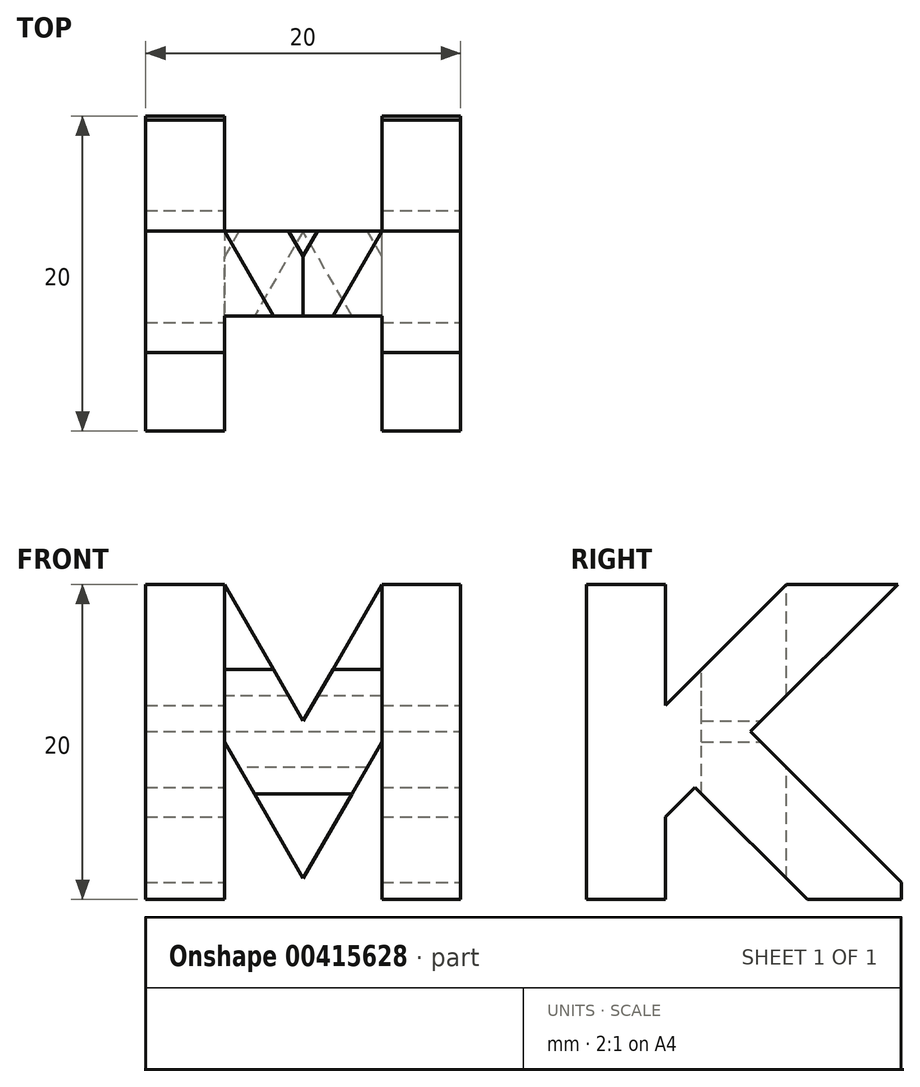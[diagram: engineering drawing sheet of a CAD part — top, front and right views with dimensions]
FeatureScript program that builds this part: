
annotation { "Feature Type Name" : "Feature", "Feature Type Description" : "" }
export const myFeature = defineFeature(function(context is Context, id is Id, definition is map)
    precondition{}
    {
        {
            var Q0;
            Q0=qCreatedBy(makeId("Front.planeOp"),FACE);
            var sketch = newSketch(context, id + "F0", { "sketchPlane" : qUnion([Q0])});
            skPoint(sketch, "E0.middle", {"position": v(0, 0) * mm});
            skLineSegment(sketch, "E1.bottom", {"start": v(-10, -10) * mm, "end": v(-5, -10) * mm});
            skLineSegment(sketch, "E1.top", {"start": v(-10, 10) * mm, "end": v(-5, 10) * mm});
            skLineSegment(sketch, "E1.left", {"start": v(-10, -10) * mm, "end": v(-10, 10) * mm});
            skLineSegment(sketch, "E1.right", {"start": v(-5, -10) * mm, "end": v(-5, 10) * mm});
            skLineSegment(sketch, "E2.bottom", {"start": v(10, 10) * mm, "end": v(5, 10) * mm});
            skLineSegment(sketch, "E2.top", {"start": v(10, -10) * mm, "end": v(5, -10) * mm});
            skLineSegment(sketch, "E2.left", {"start": v(10, 10) * mm, "end": v(10, -10) * mm});
            skLineSegment(sketch, "E2.right", {"start": v(5, 10) * mm, "end": v(5, -10) * mm});
            skLineSegment(sketch, "E3", {"start": v(5, 10) * mm, "end": v(0, 1.34) * mm});
            skLineSegment(sketch, "E4", {"start": v(0, 1.34) * mm, "end": v(-5, 10) * mm});
            skLineSegment(sketch, "E5", {"start": v(5, 0) * mm, "end": v(0, -8.66) * mm});
            skLineSegment(sketch, "E6", {"start": v(0, -8.66) * mm, "end": v(-5, 0) * mm});
            skSolve(sketch);
        }
        {
            var Q0;
            Q0 = qSketchRegion(id + "F0", true);
            extrude(context, id + "F1", {"entities" : qUnion([Q0]), "depth" : 10 * mm, "hasSecondDirection" : true, "secondDirectionOppositeDirection" : true, "secondDirectionDepth" : 10 * mm});
        }
        {
            var Q0;
            Q0=makeQuery(id+"F1.opExtrude","SWEPT_FACE",FACE,{"disambiguationData":[OSD([sQuery(id+"F0.wireOp",EDGE,"E2.left")])]});
            var sketch = newSketch(context, id + "F2", { "sketchPlane" : qUnion([Q0])});
            skLineSegment(sketch, "E7.bottom", {"start": v(-10, 10) * mm, "end": v(-5, 10) * mm});
            skLineSegment(sketch, "E7.top", {"start": v(-10, -10) * mm, "end": v(-5, -10) * mm});
            skLineSegment(sketch, "E7.left", {"start": v(-10, 10) * mm, "end": v(-10, -10) * mm});
            skLineSegment(sketch, "E7.right", {"start": v(-5, 10) * mm, "end": v(-5, -10) * mm});
            skPoint(sketch, "E8", {"position": v(10, 10) * mm});
            skLineSegment(sketch, "E9", {"start": v(10, 10) * mm, "end": v(2.7, 10) * mm});
            skLineSegment(sketch, "E10", {"start": v(10, 10.24) * mm, "end": v(10, 10) * mm});
            skLineSegment(sketch, "E11", {"start": v(2.7, 10) * mm, "end": v(-5, 2.3) * mm});
            skLineSegment(sketch, "E12", {"start": v(10, 10.24) * mm, "end": v(-5, -4.76) * mm});
            skPoint(sketch, "E13", {"position": v(10, -10) * mm});
            skLineSegment(sketch, "E14", {"start": v(10, -10) * mm, "end": v(10, -8.91) * mm});
            skLineSegment(sketch, "E15", {"start": v(10, -10) * mm, "end": v(4.02, -10) * mm});
            skLineSegment(sketch, "E16", {"start": v(10, -8.91) * mm, "end": v(0.42, 0.66) * mm});
            skLineSegment(sketch, "E17", {"start": v(4.02, -10) * mm, "end": v(-3.11, -2.87) * mm});
            skSolve(sketch);
        }
        {
            var Q0;
            Q0 = qSketchRegion(id + "F2", true);
            extrude(context, id + "F3", {"entities" : qUnion([Q0]), "oppositeDirection" : true, "depth" : 20 * mm});
        }
        {
            var Q0;
            Q0=makeQuery(id+"F3.opExtrude","SWEPT_BODY",BODY,{"disambiguationData":[OSD([sQuery(id+"F2.wireOp",EDGE,"E7.bottom"),sQuery(id+"F2.wireOp",EDGE,"E7.top"),sQuery(id+"F2.wireOp",EDGE,"E7.left"),sQuery(id+"F2.wireOp",EDGE,"E7.right"),sQuery(id+"F2.wireOp",EDGE,"E9"),sQuery(id+"F2.wireOp",EDGE,"E11"),sQuery(id+"F2.wireOp",EDGE,"E12"),sQuery(id+"F2.wireOp",EDGE,"E14"),sQuery(id+"F2.wireOp",EDGE,"E15"),sQuery(id+"F2.wireOp",EDGE,"E16"),sQuery(id+"F2.wireOp",EDGE,"E17")])]});
            var Q1;
            Q1=makeQuery(id+"F1.opExtrude","SWEPT_BODY",BODY,{"disambiguationData":[OSD([sQuery(id+"F0.wireOp",EDGE,"E1.bottom"),sQuery(id+"F0.wireOp",EDGE,"E1.top"),sQuery(id+"F0.wireOp",EDGE,"E1.left"),sQuery(id+"F0.wireOp",EDGE,"E1.right"),sQuery(id+"F0.wireOp",EDGE,"E2.bottom"),sQuery(id+"F0.wireOp",EDGE,"E2.top"),sQuery(id+"F0.wireOp",EDGE,"E2.left"),sQuery(id+"F0.wireOp",EDGE,"E2.right"),sQuery(id+"F0.wireOp",EDGE,"E3"),sQuery(id+"F0.wireOp",EDGE,"E4"),sQuery(id+"F0.wireOp",EDGE,"E5"),sQuery(id+"F0.wireOp",EDGE,"E6")])]});
            booleanBodies(context, id + "F4", {"operationType" : BooleanOperationType.INTERSECTION, "tools" : qUnion([Q0, Q1])});
        }
        {
            var Q0;
            Q0=makeQuery(id+"F3.opExtrude","SWEPT_BODY",BODY,{"disambiguationData":[OSD([sQuery(id+"F2.wireOp",EDGE,"E9"),sQuery(id+"F2.wireOp",EDGE,"E10"),sQuery(id+"F2.wireOp",EDGE,"E12")])]});
            deleteBodies(context, id + "F5", {"entities" : qUnion([Q0])});
        }
        {
            var Q0;
            {var subQ1=sQuery(id+"F2.wireOp",EDGE,"E12");var subQ3=sQuery(id+"F2.wireOp",EDGE,"E9");var subQ4=makeQuery(id+"F2.imprint","INTERSECT",VERTEX,{"derivedFrom":[subQ3,subQ1]});Q0=makeQuery(id+"F4.opBoolean","SPLIT",FACE,{"disambiguationData":[TD([makeQuery(id+"F1.opExtrude","SWEPT_FACE",FACE,{"disambiguationData":[OSD([sQuery(id+"F0.wireOp",EDGE,"E4")])]})])],"derivedFrom":makeQuery(id+"F3.opExtrude","SWEPT_FACE",FACE,{"disambiguationData":[OSD([subQ3]),TDD([makeQuery(id+"F2.imprint","IMPRINT",EDGE,{"disambiguationData":[TD([[subQ4,1.0]])],"derivedFrom":subQ3})])]})});}
            var sketch = newSketch(context, id + "F6", { "sketchPlane" : qUnion([Q0])});
            skPoint(sketch, "E18.0", {"position": v(10, 10) * mm});
            skPoint(sketch, "E18.1", {"position": v(5, -10) * mm});
            skPoint(sketch, "E18.2", {"position": v(-5, -10) * mm});
            skPoint(sketch, "E18.3", {"position": v(-10, 10) * mm});
            skLineSegment(sketch, "E19.bottom", {"start": v(10, 10) * mm, "end": v(5, 10) * mm});
            skLineSegment(sketch, "E19.top", {"start": v(10, -10) * mm, "end": v(5, -10) * mm});
            skLineSegment(sketch, "E19.left", {"start": v(10, 10) * mm, "end": v(10, -10) * mm});
            skLineSegment(sketch, "E19.right", {"start": v(5, 10) * mm, "end": v(5, -10) * mm});
            skLineSegment(sketch, "E20.bottom", {"start": v(-10, 10) * mm, "end": v(-5, 10) * mm});
            skLineSegment(sketch, "E20.top", {"start": v(-10, -10) * mm, "end": v(-5, -10) * mm});
            skLineSegment(sketch, "E20.left", {"start": v(-10, 10) * mm, "end": v(-10, -10) * mm});
            skLineSegment(sketch, "E20.right", {"start": v(-5, 10) * mm, "end": v(-5, -10) * mm});
            skLineSegment(sketch, "E21.bottom", {"start": v(5, 2.7) * mm, "end": v(-5, 2.7) * mm});
            skLineSegment(sketch, "E21.top", {"start": v(5, -2.7) * mm, "end": v(-5, -2.7) * mm});
            skLineSegment(sketch, "E21.left", {"start": v(5, 2.7) * mm, "end": v(5, -2.7) * mm});
            skLineSegment(sketch, "E21.right", {"start": v(-5, 2.7) * mm, "end": v(-5, -2.7) * mm});
            skSolve(sketch);
        }
        {
            var Q0;
            Q0 = qSketchRegion(id + "F6", true);
            extrude(context, id + "F7", {"entities" : qUnion([Q0]), "oppositeDirection" : true, "depth" : 20 * mm});
        }
        {
            var Q0;
            Q0=makeQuery(id+"F4.opBoolean","INTERSECT",BODY,{"derivedFrom":[makeQuery(id+"F1.opExtrude","SWEPT_BODY",BODY,{"disambiguationData":[OSD([sQuery(id+"F0.wireOp",EDGE,"E1.bottom"),sQuery(id+"F0.wireOp",EDGE,"E1.top"),sQuery(id+"F0.wireOp",EDGE,"E1.left"),sQuery(id+"F0.wireOp",EDGE,"E1.right"),sQuery(id+"F0.wireOp",EDGE,"E2.bottom"),sQuery(id+"F0.wireOp",EDGE,"E2.top"),sQuery(id+"F0.wireOp",EDGE,"E2.left"),sQuery(id+"F0.wireOp",EDGE,"E2.right"),sQuery(id+"F0.wireOp",EDGE,"E3"),sQuery(id+"F0.wireOp",EDGE,"E4"),sQuery(id+"F0.wireOp",EDGE,"E5"),sQuery(id+"F0.wireOp",EDGE,"E6")])]}),makeQuery(id+"F3.opExtrude","SWEPT_BODY",BODY,{"disambiguationData":[OSD([sQuery(id+"F2.wireOp",EDGE,"E7.bottom"),sQuery(id+"F2.wireOp",EDGE,"E7.top"),sQuery(id+"F2.wireOp",EDGE,"E7.left"),sQuery(id+"F2.wireOp",EDGE,"E7.right"),sQuery(id+"F2.wireOp",EDGE,"E9"),sQuery(id+"F2.wireOp",EDGE,"E11"),sQuery(id+"F2.wireOp",EDGE,"E12"),sQuery(id+"F2.wireOp",EDGE,"E14"),sQuery(id+"F2.wireOp",EDGE,"E15"),sQuery(id+"F2.wireOp",EDGE,"E16"),sQuery(id+"F2.wireOp",EDGE,"E17")])]})]});
            var Q1;
            Q1=makeQuery(id+"F7.opExtrude","SWEPT_BODY",BODY,{"disambiguationData":[OSD([sQuery(id+"F6.wireOp",EDGE,"E19.bottom"),sQuery(id+"F6.wireOp",EDGE,"E19.top"),sQuery(id+"F6.wireOp",EDGE,"E19.left"),sQuery(id+"F6.wireOp",EDGE,"E19.right"),sQuery(id+"F6.wireOp",EDGE,"E20.bottom"),sQuery(id+"F6.wireOp",EDGE,"E20.top"),sQuery(id+"F6.wireOp",EDGE,"E20.left"),sQuery(id+"F6.wireOp",EDGE,"E20.right"),sQuery(id+"F6.wireOp",EDGE,"E21.bottom"),sQuery(id+"F6.wireOp",EDGE,"E21.top")])]});
            booleanBodies(context, id + "F8", {"operationType" : BooleanOperationType.INTERSECTION, "tools" : qUnion([Q0, Q1])});
        }
    });
